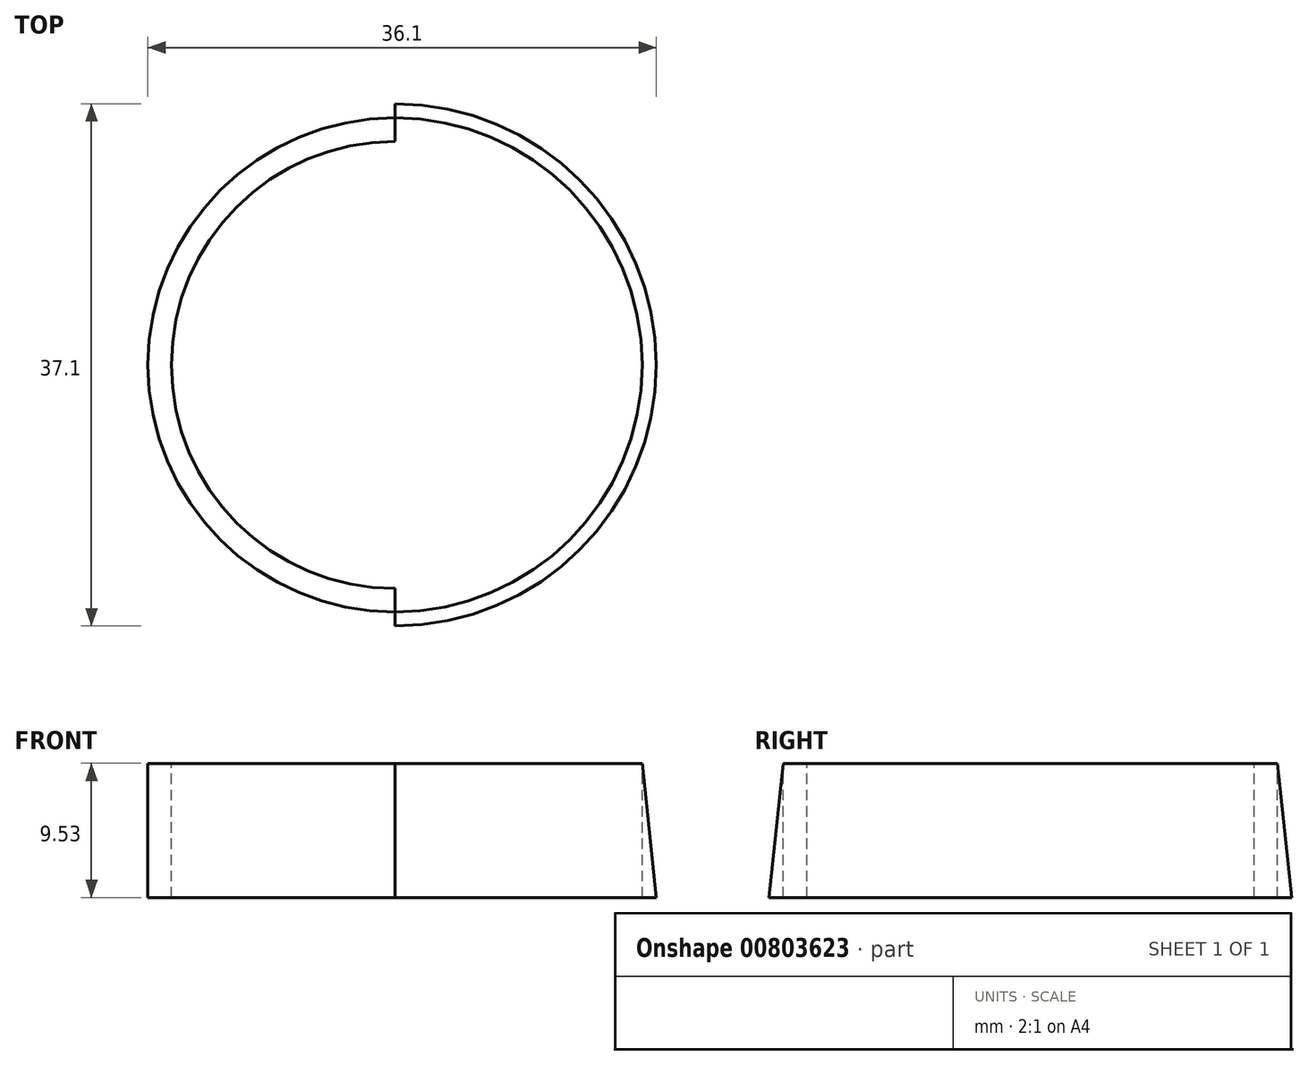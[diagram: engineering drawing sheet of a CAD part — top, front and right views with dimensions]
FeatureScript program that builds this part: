
annotation { "Feature Type Name" : "Feature", "Feature Type Description" : "" }
export const myFeature = defineFeature(function(context is Context, id is Id, definition is map)
    precondition{}
    {
        {
            var Q0;
            Q0=qCreatedBy(makeId("Top.planeOp"),FACE);
            var sketch = newSketch(context, id + "F0", { "sketchPlane" : qUnion([Q0])});
            skCircle(sketch, "E0", {"center": v(0, 0) * mm, "radius": 18.55 * mm});
            skSolve(sketch);
        }
        {
            var Q0;
            Q0=makeQuery(id+"F0.imprint","IMPRINT",FACE,{"disambiguationData":[TD([[makeQuery(id+"F0.imprint","IMPRINT",EDGE,{"derivedFrom":sQuery(id+"F0.wireOp",EDGE,"E0")}),1.0]])]});
            extrude(context, id + "F1", {"entities" : qUnion([Q0]), "depth" : 9.52 * mm, "offsetDistance" : 25.4 * mm, "hasDraft" : true, "draftAngle" : 6 * degree, "draftPullDirection" : true});
        }
        {
            var Q0;
            Q0=makeQuery(id+"F1.opExtrude","CAP_FACE",FACE,{"disambiguationData":[OSD([sQuery(id+"F0.wireOp",EDGE,"E0")])],"isStart":false});
            var sketch = newSketch(context, id + "F2", { "sketchPlane" : qUnion([Q0])});
            skCircle(sketch, "E1.0", {"center": v(0, 0) * mm, "radius": 17.55 * mm});
            skCircle(sketch, "E2", {"center": v(0, 0) * mm, "radius": 15.88 * mm});
            skLineSegment(sketch, "E3", {"start": v(0, 17.55) * mm, "end": v(0, -17.55) * mm});
            skLineSegment(sketch, "E4.bottom", {"start": v(0, 24.5) * mm, "end": v(-20.4, 24.5) * mm});
            skLineSegment(sketch, "E4.top", {"start": v(0, -25.33) * mm, "end": v(-20.4, -25.33) * mm});
            skLineSegment(sketch, "E4.left", {"start": v(0, 24.5) * mm, "end": v(0, -25.33) * mm});
            skLineSegment(sketch, "E4.right", {"start": v(-20.4, 24.5) * mm, "end": v(-20.4, -25.33) * mm});
            skSolve(sketch);
        }
        {
            var Q0;
            {var subQ0=sQuery(id+"F2.wireOp",EDGE,"E4.left");var subQ1=sQuery(id+"F2.wireOp",EDGE,"E2");var subQ2=makeQuery(id+"F2.imprint","INTERSECT",VERTEX,{"disambiguationData":[OD(0.0)],"derivedFrom":[subQ1,subQ0]});Q0=makeQuery(id+"F2.imprint","IMPRINT",FACE,{"disambiguationData":[TD([[makeQuery(id+"F2.imprint","IMPRINT",EDGE,{"disambiguationData":[TD([[subQ2,1.0]])],"derivedFrom":subQ1}),1.0]])]});}
            var Q1;
            {var subQ0=sQuery(id+"F2.wireOp",EDGE,"E4.left");var subQ1=sQuery(id+"F2.wireOp",EDGE,"E2");var subQ2=makeQuery(id+"F2.imprint","INTERSECT",VERTEX,{"disambiguationData":[OD(0.0)],"derivedFrom":[subQ1,subQ0]});Q1=makeQuery(id+"F2.imprint","IMPRINT",FACE,{"disambiguationData":[TD([[makeQuery(id+"F2.imprint","IMPRINT",EDGE,{"disambiguationData":[TD([[subQ2,-1.0]])],"derivedFrom":subQ1}),1.0]])]});}
            var Q2;
            {var subQ0=sQuery(id+"F2.wireOp",EDGE,"E4.left");var subQ1=sQuery(id+"F2.wireOp",EDGE,"E1.0");var subQ2=makeQuery(id+"F2.imprint","INTERSECT",VERTEX,{"disambiguationData":[OD(0.0)],"derivedFrom":[subQ1,subQ0]});Q2=makeQuery(id+"F2.imprint","IMPRINT",FACE,{"disambiguationData":[TD([[makeQuery(id+"F2.imprint","IMPRINT",EDGE,{"disambiguationData":[TD([[subQ2,-1.0]])],"derivedFrom":subQ1}),1.0]])]});}
            var Q3;
            {var subQ1=sQuery(id+"F2.wireOp",EDGE,"E4.bottom");Q3=makeQuery(id+"F2.imprint","IMPRINT",FACE,{"disambiguationData":[TD([[makeQuery(id+"F2.imprint","IMPRINT",EDGE,{"derivedFrom":subQ1}),1.0]])]});}
            extrude(context, id + "F3", {"entities" : qUnion([Q0, Q1, Q2, Q3]), "operationType" : NewBodyOperationType.REMOVE, "oppositeDirection" : true, "depth" : 25.4 * mm, "offsetDistance" : 25.4 * mm});
        }
    });
